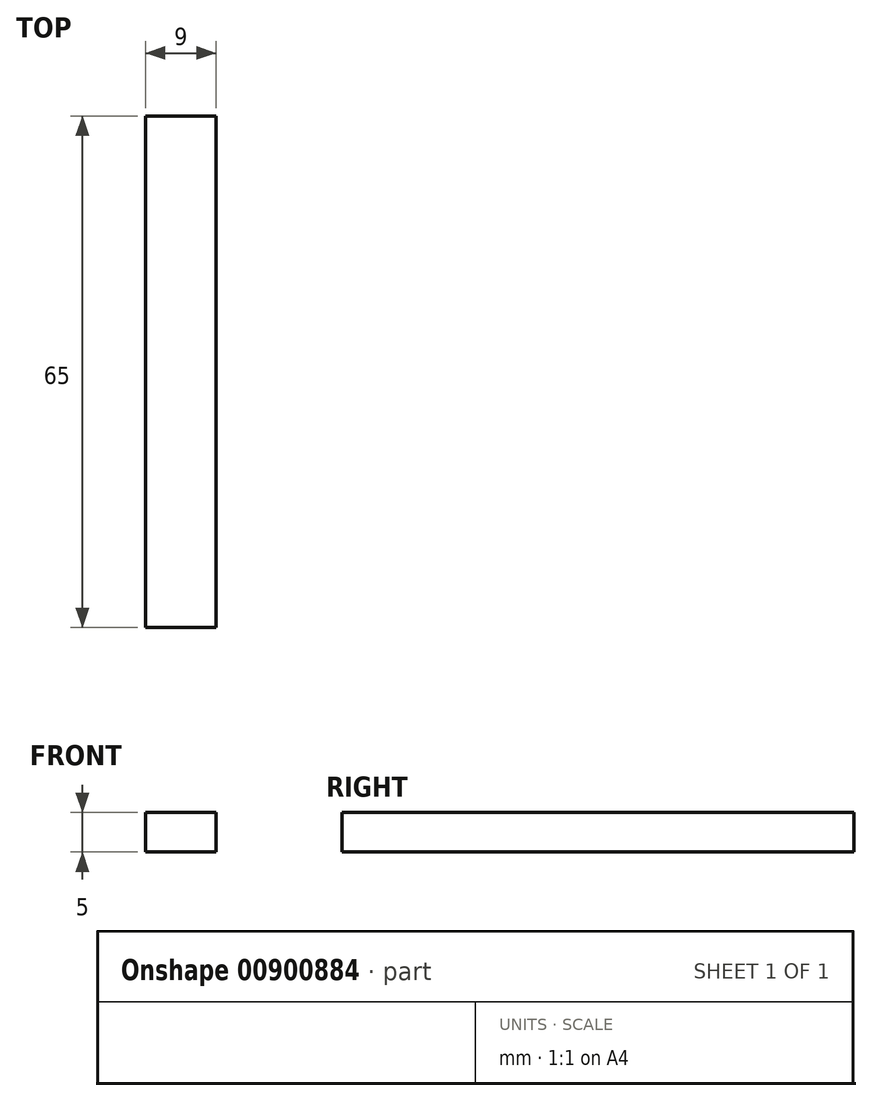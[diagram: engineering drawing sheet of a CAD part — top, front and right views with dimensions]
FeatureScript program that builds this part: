
annotation { "Feature Type Name" : "Feature", "Feature Type Description" : "" }
export const myFeature = defineFeature(function(context is Context, id is Id, definition is map)
    precondition{}
    {
        {
            var Q0;
            Q0=qCreatedBy(makeId("Top.planeOp"),FACE);
            var sketch = newSketch(context, id + "F0", { "sketchPlane" : qUnion([Q0])});
            skLineSegment(sketch, "E0.bottom", {"start": v(0, 0) * mm, "end": v(-9, 0) * mm});
            skLineSegment(sketch, "E0.top", {"start": v(0, 65) * mm, "end": v(-9, 65) * mm});
            skLineSegment(sketch, "E0.left", {"start": v(0, 0) * mm, "end": v(0, 65) * mm});
            skLineSegment(sketch, "E0.right", {"start": v(-9, 0) * mm, "end": v(-9, 65) * mm});
            skSolve(sketch);
        }
        {
            var Q0;
            Q0 = qSketchRegion(id + "F0", true);
            extrude(context, id + "F1", {"entities" : qUnion([Q0]), "depth" : 5 * mm, "offsetDistance" : 25 * mm});
        }
    });
